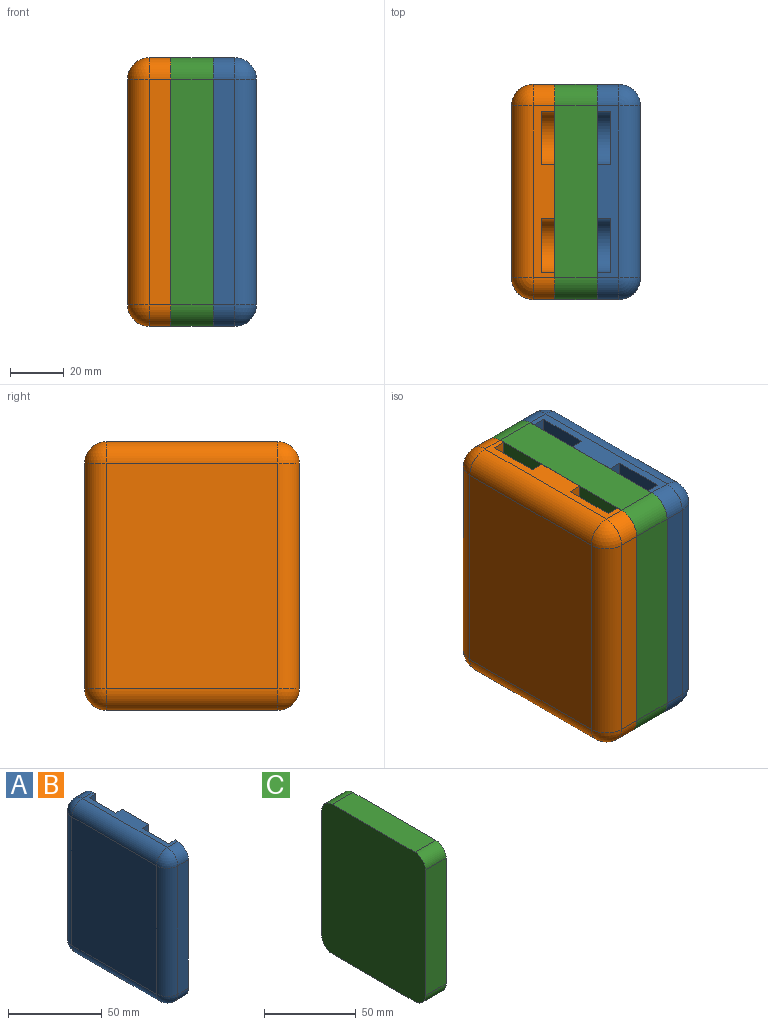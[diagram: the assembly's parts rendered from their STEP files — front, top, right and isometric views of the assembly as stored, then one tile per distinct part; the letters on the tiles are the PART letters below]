
ASSEMBLY  parts=3 mates=1
PART A: 26 faces, bbox 16x80x100 mm
  f0: plane 100x80mm, normal (1,0,0), area 4430.9mm2, adj f1,f2,f3,f4,f6,f7,f8,f10
  f1: plane 64x8mm, normal (0,0,1), area 312mm2, adj f0,f6,f8,f9,f10,f12,f13,f19
  f2: plane 84x8mm, normal (0,-1,0), area 672mm2, adj f0,f16,f22,f25
  f3: plane 64x8mm, normal (0,0,-1), area 512mm2, adj f0,f14,f16,f17
  f4: plane 84x8mm, normal (0,1,0), area 672mm2, adj f0,f14,f18,f19
  f5: plane 84x64mm, normal (-1,0,0), area 5376mm2, adj f17,f18,f22,f23
  f6: plane 80x5mm, normal (0,1,0), area 400mm2, adj f0,f1,f7,f9
  f7: cylinder r=10mm len=20mm, axis (1,0,0), area 157.1mm2, adj f0,f6,f8,f9
  f8: plane 80x5mm, normal (0,-1,0), area 400mm2, adj f0,f1,f7,f9
  f9: plane 90x20mm, normal (1,0,0), area 1757.1mm2, adj f1,f6,f7,f8
  f10: plane 80x5mm, normal (0,1,0), area 400mm2, adj f0,f1,f11,f13
  f11: cylinder r=10mm len=20mm, axis (1,0,0), area 157.1mm2, adj f0,f10,f12,f13
  f12: plane 80x5mm, normal (0,-1,0), area 400mm2, adj f0,f1,f11,f13
  f13: plane 90x20mm, normal (1,0,0), area 1757.1mm2, adj f1,f10,f11,f12
  f14: cylinder r=8mm len=8mm, axis (1,0,0), area 100.5mm2, adj f0,f3,f4,f15
  f15: sphere r=8mm, area 100.5mm2, adj f14,f17,f18
  f16: cylinder r=8mm len=8mm, axis (-1,0,0), area 100.5mm2, adj f0,f2,f3,f20
  f17: cylinder r=8mm len=64mm, axis (0,-1,0), area 804.2mm2, adj f3,f5,f15,f20
  f18: cylinder r=8mm len=84mm, axis (0,0,-1), area 1055.6mm2, adj f4,f5,f15,f21
  f19: cylinder r=8mm len=8mm, axis (-1,0,0), area 100.5mm2, adj f0,f1,f4,f21
  f20: sphere r=8mm, area 100.5mm2, adj f16,f17,f22
  f21: sphere r=8mm, area 100.5mm2, adj f18,f19,f23
  f22: cylinder r=8mm len=84mm, axis (0,0,1), area 1055.6mm2, adj f2,f5,f20,f24
  f23: cylinder r=8mm len=64mm, axis (0,1,0), area 804.2mm2, adj f1,f5,f21,f24
  f24: sphere r=8mm, area 100.5mm2, adj f22,f23,f25
  f25: cylinder r=8mm len=8mm, axis (1,0,0), area 100.5mm2, adj f0,f1,f2,f24
PART B: same geometry as A
PART C: 10 faces, bbox 16x80x100 mm
  f0: plane 64x16mm, normal (0,0,1), area 1024mm2, adj f4,f5,f6,f9
  f1: plane 84x16mm, normal (0,-1,0), area 1344mm2, adj f4,f5,f6,f7
  f2: plane 64x16mm, normal (0,0,-1), area 1024mm2, adj f4,f5,f7,f8
  f3: plane 84x16mm, normal (0,1,0), area 1344mm2, adj f4,f5,f8,f9
  f4: plane 100x80mm, normal (1,0,0), area 7945.1mm2, adj f0,f1,f2,f3,f6,f7,f8,f9
  f5: plane 100x80mm, normal (-1,0,0), area 7945.1mm2, adj f0,f1,f2,f3,f6,f7,f8,f9
  f6: cylinder r=8mm len=16mm, axis (-1,0,0), area 201.1mm2, adj f0,f1,f4,f5
  f7: cylinder r=8mm len=16mm, axis (1,0,0), area 201.1mm2, adj f1,f2,f4,f5
  f8: cylinder r=8mm len=16mm, axis (-1,0,0), area 201.1mm2, adj f2,f3,f4,f5
  f9: cylinder r=8mm len=16mm, axis (1,0,0), area 201.1mm2, adj f0,f3,f4,f5
PLACE A rot(axis=(0,0,1),180deg) t=(16,80,0)mm
PLACE B at identity fixed
PLACE C at identity fixed
MATE fastened A.f0 <-> C.f4  axis (-1,0,0) through (16,40,100)mm
